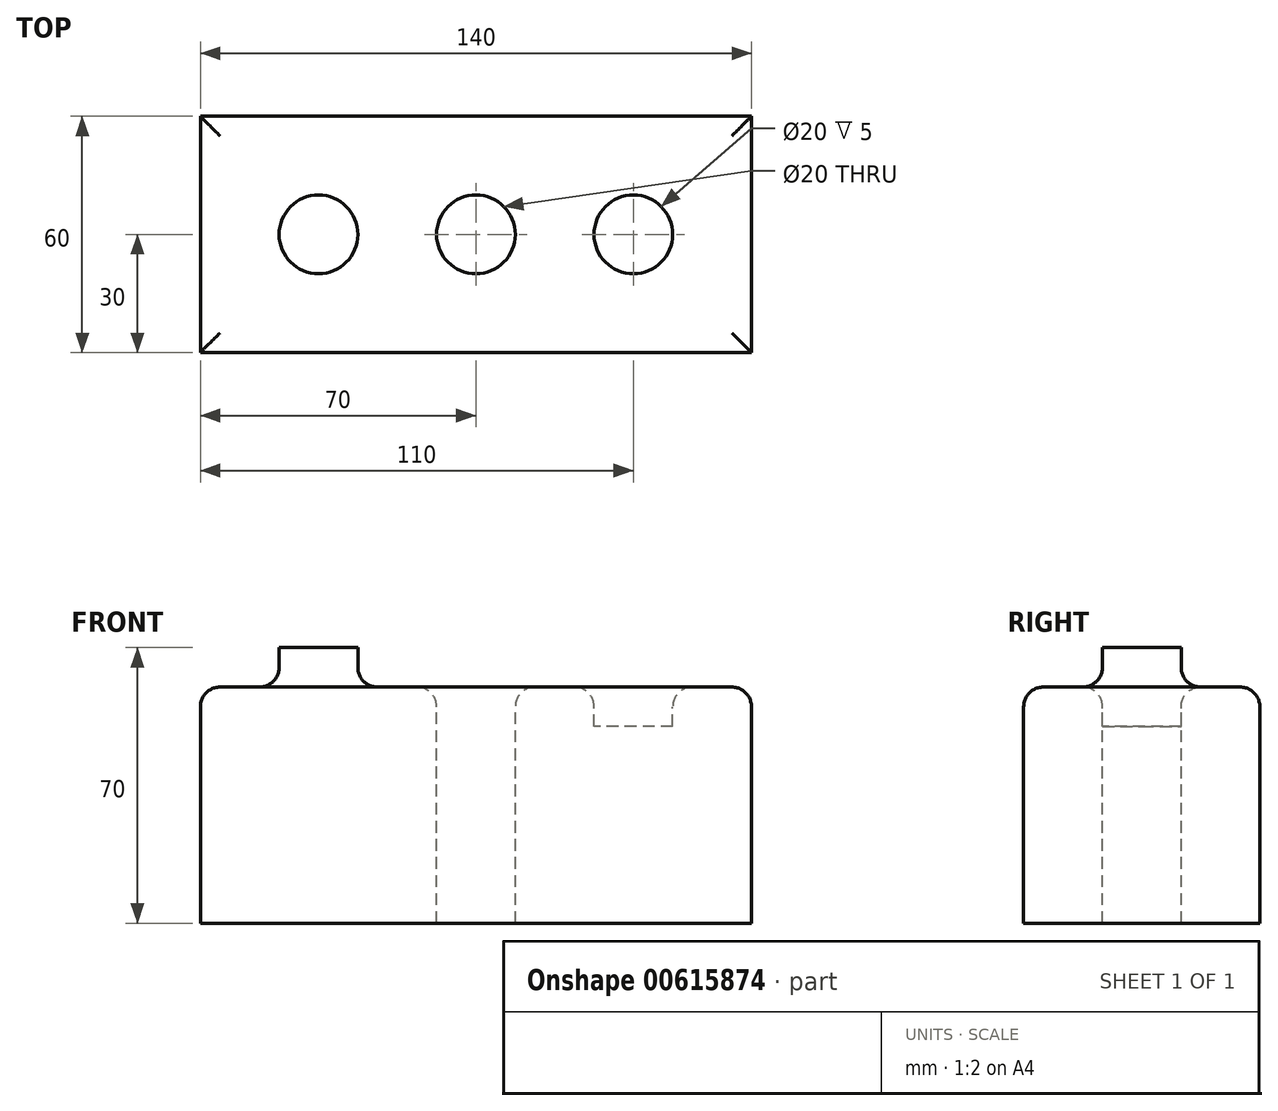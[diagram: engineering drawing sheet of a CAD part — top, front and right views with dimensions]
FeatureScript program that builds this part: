
annotation { "Feature Type Name" : "Feature", "Feature Type Description" : "" }
export const myFeature = defineFeature(function(context is Context, id is Id, definition is map)
    precondition{}
    {
        {
            var Q0;
            Q0=qCreatedBy(makeId("Top.planeOp"),FACE);
            var sketch = newSketch(context, id + "F0", { "sketchPlane" : qUnion([Q0])});
            skLineSegment(sketch, "E0.bottom", {"start": v(70, -30) * mm, "end": v(-70, -30) * mm});
            skLineSegment(sketch, "E0.top", {"start": v(70, 30) * mm, "end": v(-70, 30) * mm});
            skLineSegment(sketch, "E0.left", {"start": v(70, -30) * mm, "end": v(70, 30) * mm});
            skLineSegment(sketch, "E0.right", {"start": v(-70, -30) * mm, "end": v(-70, 30) * mm});
            skPoint(sketch, "E0.middle", {"position": v(0, 0) * mm});
            skSolve(sketch);
        }
        {
            var Q0;
            Q0 = qSketchRegion(id + "F0", true);
            extrude(context, id + "F1", {"entities" : qUnion([Q0]), "depth" : 60 * mm, "offsetDistance" : 25 * mm});
        }
        {
            var Q0;
            Q0=makeQuery(id+"F1.opExtrude","CAP_FACE",FACE,{"disambiguationData":[OSD([sQuery(id+"F0.wireOp",EDGE,"E0.bottom"),sQuery(id+"F0.wireOp",EDGE,"E0.top"),sQuery(id+"F0.wireOp",EDGE,"E0.left"),sQuery(id+"F0.wireOp",EDGE,"E0.right")])],"isStart":false});
            var sketch = newSketch(context, id + "F2", { "sketchPlane" : qUnion([Q0])});
            skCircle(sketch, "E1", {"center": v(-40, 0) * mm, "radius": 10 * mm});
            skSolve(sketch);
        }
        {
            var Q0;
            Q0=makeQuery(id+"F2.imprint","IMPRINT",FACE,{"disambiguationData":[TD([[makeQuery(id+"F2.imprint","IMPRINT",EDGE,{"derivedFrom":sQuery(id+"F2.wireOp",EDGE,"E1")}),-1.0]])]});
            var sketch = newSketch(context, id + "F3", { "sketchPlane" : qUnion([Q0])});
            skCircle(sketch, "E2", {"center": v(40, 0) * mm, "radius": 10 * mm});
            skSolve(sketch);
        }
        {
            var Q0;
            Q0=makeQuery(id+"F2.imprint","IMPRINT",FACE,{"disambiguationData":[TD([[makeQuery(id+"F2.imprint","IMPRINT",EDGE,{"derivedFrom":sQuery(id+"F2.wireOp",EDGE,"E1")}),-1.0]])]});
            var sketch = newSketch(context, id + "F4", { "sketchPlane" : qUnion([Q0])});
            skCircle(sketch, "E3", {"center": v(0, 0) * mm, "radius": 10 * mm});
            skSolve(sketch);
        }
        {
            var Q0;
            Q0 = qSketchRegion(id + "F2", true);
            extrude(context, id + "F5", {"entities" : qUnion([Q0]), "operationType" : NewBodyOperationType.ADD, "depth" : 10 * mm, "offsetDistance" : 25 * mm});
        }
        {
            var Q0;
            Q0 = qSketchRegion(id + "F3", true);
            extrude(context, id + "F6", {"entities" : qUnion([Q0]), "operationType" : NewBodyOperationType.REMOVE, "oppositeDirection" : true, "depth" : 10 * mm, "offsetDistance" : 25 * mm});
        }
        {
            var Q0;
            Q0 = qSketchRegion(id + "F4", true);
            extrude(context, id + "F7", {"entities" : qUnion([Q0]), "operationType" : NewBodyOperationType.REMOVE, "oppositeDirection" : true, "depth" : 79.5 * mm, "offsetDistance" : 25 * mm});
        }
        {
            var Q0;
            Q0=makeQuery(id+"F1.opExtrude","CAP_EDGE",EDGE,{"disambiguationData":[OSD([sQuery(id+"F0.wireOp",EDGE,"E0.right")])],"isStart":false});
            var Q1;
            Q1=makeQuery(id+"F1.opExtrude","CAP_FACE",FACE,{"disambiguationData":[OSD([sQuery(id+"F0.wireOp",EDGE,"E0.bottom"),sQuery(id+"F0.wireOp",EDGE,"E0.top"),sQuery(id+"F0.wireOp",EDGE,"E0.left"),sQuery(id+"F0.wireOp",EDGE,"E0.right")])],"isStart":false});
            var Q2;
            Q2=makeQuery(id+"F1.opExtrude","CAP_EDGE",EDGE,{"disambiguationData":[OSD([sQuery(id+"F0.wireOp",EDGE,"E0.left")])],"isStart":false});
            var Q3;
            Q3=makeQuery(id+"F1.opExtrude","CAP_EDGE",EDGE,{"disambiguationData":[OSD([sQuery(id+"F0.wireOp",EDGE,"E0.top")])],"isStart":false});
            fillet(context, id + "F8", {"entities" : qUnion([Q0, Q1, Q2, Q3]), "radius" : 5 * mm, "tangentPropagation" : true, "allowEdgeOverflow" : false});
        }
    });
